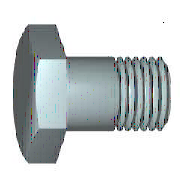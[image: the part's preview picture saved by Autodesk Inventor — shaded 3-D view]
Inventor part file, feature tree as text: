
AUTODESK INVENTOR PART (.ipt)
format: ipt  version: 2021 (Build 250183000, 183)  size: 191,488 bytes
history: native  units: mm (DEFAULTED — no unit token found)
features: sketch x3, extrude x1, chamfer x1, plane x1
ambient origin geometry x7: Origin, YZ Plane, XZ Plane, X Axis, Y Axis, Z Axis, Center Point
bodies: Solid1 (feature_tree), Body (feature_tree)
feature tree (6):
  extrude  "Head"  Depth=22.0mm
  chamfer  "Chamfer1"  Distance=4.7mm
  plane  "Work Plane1"
  sketch  "Sketch1"  dims[d0=60.0mm d1=22.0mm]
  sketch  "Sketch2"  dims[d2=8.0mm]
  sketch  "Sketch4"  dims[d12=90.0deg d3=4.7mm d4=0.0mm d5=30.0deg d21=90.0deg d6=0.766813mm d7=0.766912mm d8=0.0mm d9=0.6001mm d10=11.63mm d11=13.0mm d13=0.766912mm d14=8.0mm d15=22.0mm d16=0.0mm d19=13.0mm d55=45.0deg d57=0.0mm d58=0.0mm]
